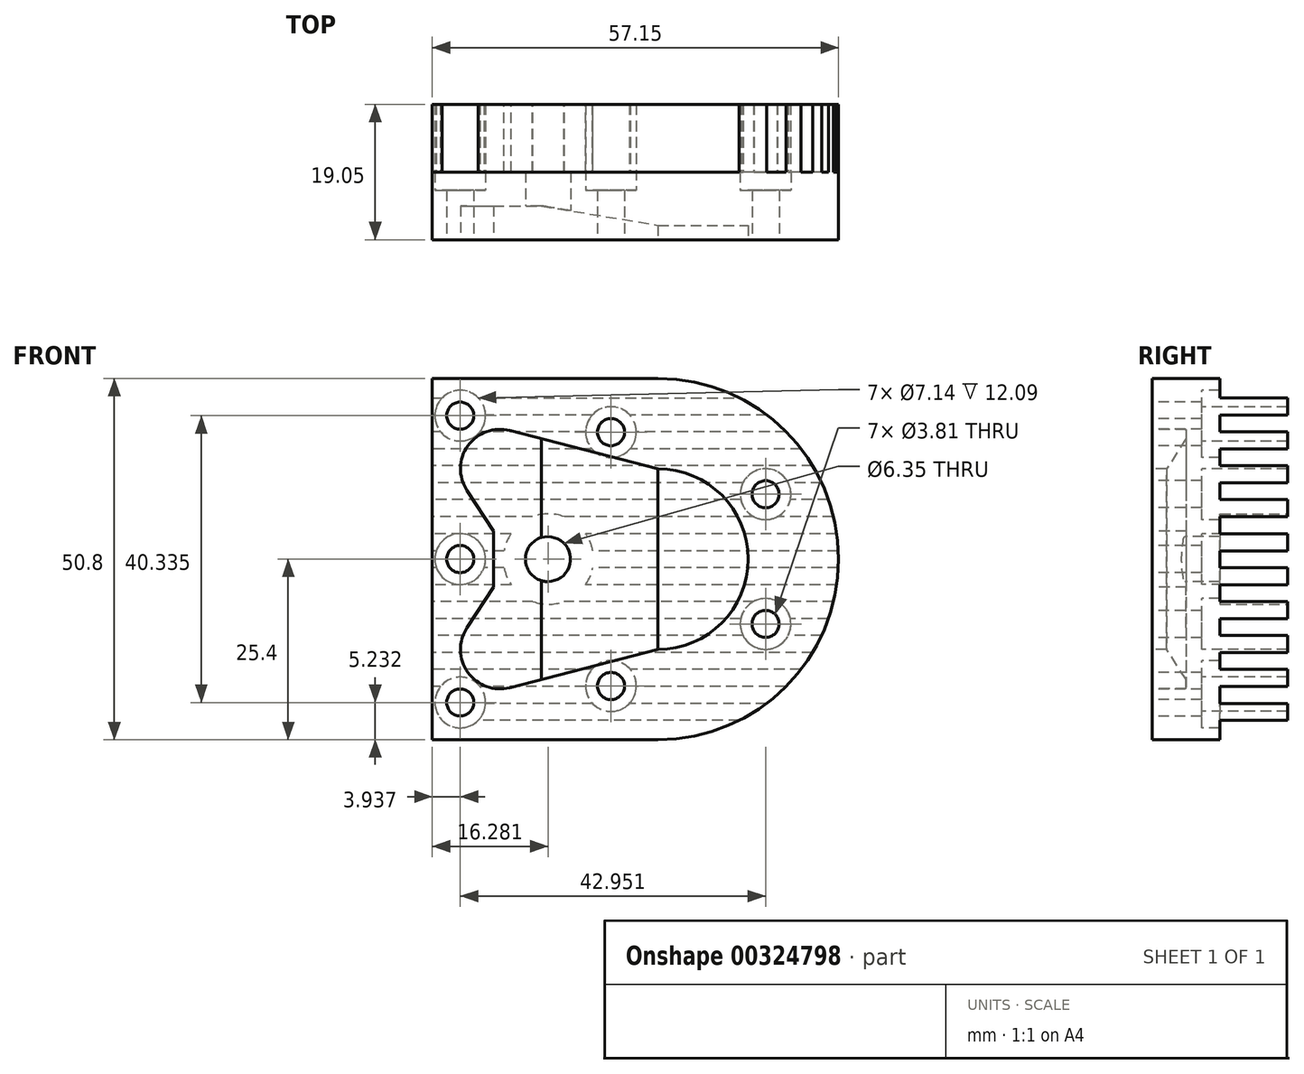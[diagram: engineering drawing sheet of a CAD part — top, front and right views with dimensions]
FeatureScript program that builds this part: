
annotation { "Feature Type Name" : "Feature", "Feature Type Description" : "" }
export const myFeature = defineFeature(function(context is Context, id is Id, definition is map)
    precondition{}
    {
        {
            var Q0;
            Q0=qCreatedBy(makeId("Front.planeOp"),FACE);
            var sketch = newSketch(context, id + "F0", { "sketchPlane" : qUnion([Q0])});
            skArc(sketch, "E0", {"start": v(0, -25.4) * mm, "mid": v(25.4, 0) * mm, "end": v(0, 25.4) * mm});
            skLineSegment(sketch, "E1", {"start": v(0, 25.4) * mm, "end": v(-31.75, 25.4) * mm});
            skLineSegment(sketch, "E2", {"start": v(0, -25.4) * mm, "end": v(-31.75, -25.4) * mm});
            skLineSegment(sketch, "E3", {"start": v(-31.75, 25.4) * mm, "end": v(-31.75, -25.4) * mm});
            skSolve(sketch);
        }
        {
            var Q0;
            Q0=makeQuery(id+"F0.imprint","IMPRINT",FACE,{"disambiguationData":[TD([[makeQuery(id+"F0.imprint","IMPRINT",EDGE,{"derivedFrom":sQuery(id+"F0.wireOp",EDGE,"E0")}),1.0]])]});
            extrude(context, id + "F1", {"entities" : qUnion([Q0]), "depth" : 19.05 * mm, "offsetDistance" : 25.4 * mm});
        }
        {
            var Q0;
            Q0=makeQuery(id+"F1.opExtrude","CAP_FACE",FACE,{"disambiguationData":[OSD([sQuery(id+"F0.wireOp",EDGE,"E0"),sQuery(id+"F0.wireOp",EDGE,"E1"),sQuery(id+"F0.wireOp",EDGE,"E2"),sQuery(id+"F0.wireOp",EDGE,"E3")])],"isStart":false});
            var sketch = newSketch(context, id + "F2", { "sketchPlane" : qUnion([Q0])});
            skArc(sketch, "E4", {"start": v(0, -12.7) * mm, "mid": v(12.7, 0) * mm, "end": v(0, 12.7) * mm});
            skLineSegment(sketch, "E5", {"start": v(0, 12.7) * mm, "end": v(0, -12.7) * mm});
            skSolve(sketch);
        }
        {
            var Q0;
            Q0=makeQuery(id+"F2.imprint","IMPRINT",FACE,{"disambiguationData":[TD([[makeQuery(id+"F2.imprint","IMPRINT",EDGE,{"derivedFrom":sQuery(id+"F2.wireOp",EDGE,"E4")}),1.0]])]});
            extrude(context, id + "F3", {"entities" : qUnion([Q0]), "operationType" : NewBodyOperationType.REMOVE, "oppositeDirection" : true, "depth" : 2.03 * mm, "offsetDistance" : 25.4 * mm});
        }
        {
            var Q0;
            Q0=makeQuery(id+"F3.boolean.opBoolean","COPY",EDGE,{"derivedFrom":makeQuery(id+"F3.opExtrude","CAP_EDGE",EDGE,{"disambiguationData":[OSD([sQuery(id+"F2.wireOp",EDGE,"E5")])],"isStart":false})});
            cPlane(context, id + "F4", {"entities" : qUnion([Q0]), "cplaneType" : CPlaneType.LINE_ANGLE, "offset" : 25.4 * mm, "angle" : 99.5 * degree, "width" : 152.4 * mm, "height" : 152.4 * mm});
        }
        {
            var Q0;
            Q0=makeQuery(id+"F1.opExtrude","CAP_FACE",FACE,{"disambiguationData":[OSD([sQuery(id+"F0.wireOp",EDGE,"E0"),sQuery(id+"F0.wireOp",EDGE,"E1"),sQuery(id+"F0.wireOp",EDGE,"E2"),sQuery(id+"F0.wireOp",EDGE,"E3")])],"isStart":false});
            var sketch = newSketch(context, id + "F5", { "sketchPlane" : qUnion([Q0])});
            skLineSegment(sketch, "E6", {"start": v(-22.23, 28.17) * mm, "end": v(-22.22, -26.85) * mm, "construction": true});
            skLineSegment(sketch, "E7", {"start": v(0, 12.7) * mm, "end": v(-42.37, 12.7) * mm, "construction": true});
            skLineSegment(sketch, "E8.MirrorCS", {"start": v(0, -12.7) * mm, "end": v(-42.37, -12.7) * mm, "construction": true});
            skArc(sketch, "E9", {"start": v(-20.84, 18.07) * mm, "mid": v(-26.74, 15.93) * mm, "end": v(-26.87, 9.66) * mm});
            skArc(sketch, "E10", {"start": v(-26.87, -9.66) * mm, "mid": v(-26.74, -15.93) * mm, "end": v(-20.84, -18.07) * mm});
            skLineSegment(sketch, "E11", {"start": v(-16.38, 30.43) * mm, "end": v(-16.38, -33.46) * mm, "construction": true});
            skLineSegment(sketch, "E12", {"start": v(-20.84, 18.07) * mm, "end": v(0, 12.7) * mm});
            skLineSegment(sketch, "E13.MirrorCS", {"start": v(-20.84, -18.07) * mm, "end": v(0, -12.7) * mm});
            skLineSegment(sketch, "E14", {"start": v(-23.11, 32.03) * mm, "end": v(-23.11, -31.77) * mm, "construction": true});
            skLineSegment(sketch, "E15", {"start": v(-23.11, 3.92) * mm, "end": v(-23.11, -3.92) * mm});
            skLineSegment(sketch, "E16", {"start": v(-26.87, 9.66) * mm, "end": v(-23.11, 3.92) * mm});
            skLineSegment(sketch, "E17.MirrorCS", {"start": v(-26.87, -9.66) * mm, "end": v(-23.11, -3.92) * mm});
            skLineSegment(sketch, "E18", {"start": v(-16.38, 16.92) * mm, "end": v(-16.38, -16.92) * mm});
            skSolve(sketch);
        }
        {
            var Q0;
            {var subQ4=sQuery(id+"F5.wireOp",EDGE,"E9");Q0=makeQuery(id+"F5.imprint","IMPRINT",FACE,{"disambiguationData":[TD([[makeQuery(id+"F5.imprint","IMPRINT",EDGE,{"derivedFrom":subQ4}),1.0]])]});}
            extrude(context, id + "F6", {"entities" : qUnion([Q0]), "operationType" : NewBodyOperationType.REMOVE, "oppositeDirection" : true, "depth" : 4.78 * mm, "offsetDistance" : 25.4 * mm});
        }
        {
            var Q0;
            {var subQ3=sQuery(id+"F5.wireOp",EDGE,"E18");Q0=makeQuery(id+"F5.imprint","IMPRINT",FACE,{"disambiguationData":[TD([[makeQuery(id+"F5.imprint","IMPRINT",EDGE,{"derivedFrom":subQ3}),1.0]])]});}
            var Q1;
            Q1=qCreatedBy(id+"F4.planeOp",FACE);
            extrude(context, id + "F7", {"entities" : qUnion([Q0]), "operationType" : NewBodyOperationType.REMOVE, "endBound" : BoundingType.UP_TO_SURFACE, "oppositeDirection" : true, "depth" : 25.4 * mm, "endBoundEntityFace" : qUnion([Q1]), "offsetDistance" : 25.4 * mm});
        }
        {
            var Q0;
            Q0=makeQuery(id+"F0.imprint","IMPRINT",FACE,{"disambiguationData":[TD([[makeQuery(id+"F0.imprint","IMPRINT",EDGE,{"derivedFrom":sQuery(id+"F0.wireOp",EDGE,"E0")}),1.0]])]});
            var sketch = newSketch(context, id + "F8", { "sketchPlane" : qUnion([Q0])});
            skPoint(sketch, "E19", {"position": v(-27.81, 20.17) * mm});
            skPoint(sketch, "E20", {"position": v(-6.6, 17.86) * mm});
            skPoint(sketch, "E21", {"position": v(15.14, 9.12) * mm});
            skPoint(sketch, "E22", {"position": v(15.14, -9.12) * mm});
            skPoint(sketch, "E23", {"position": v(-6.6, -17.86) * mm});
            skPoint(sketch, "E24", {"position": v(-27.81, -20.17) * mm});
            skPoint(sketch, "E25", {"position": v(-27.81, 0) * mm});
            skSolve(sketch);
        }
        {
            var Q0;
            Q0=sQuery(id+"F8.wireOp",VERTEX,"E19");
            var Q1;
            Q1=sQuery(id+"F8.wireOp",VERTEX,"E20");
            var Q2;
            Q2=sQuery(id+"F8.wireOp",VERTEX,"E21");
            var Q3;
            Q3=sQuery(id+"F8.wireOp",VERTEX,"E22");
            var Q4;
            Q4=sQuery(id+"F8.wireOp",VERTEX,"E23");
            var Q5;
            Q5=sQuery(id+"F8.wireOp",VERTEX,"E24");
            var Q6;
            Q6=sQuery(id+"F8.wireOp",VERTEX,"E25");
            var Q7;
            Q7=makeQuery(id+"F1.opExtrude","SWEPT_BODY",BODY,{"disambiguationData":[OSD([sQuery(id+"F0.wireOp",EDGE,"E0"),sQuery(id+"F0.wireOp",EDGE,"E1"),sQuery(id+"F0.wireOp",EDGE,"E2"),sQuery(id+"F0.wireOp",EDGE,"E3")])]});
            hole(context, id + "F9", {"style" : HoleStyle.C_BORE, "endStyle" : HoleEndStyle.THROUGH, "oppositeDirection" : true, "holeDiameter" : 3.8 * mm, "cBoreDiameter" : 7.14 * mm, "cBoreDepth" : 12.1 * mm, "majorDiameter" : 6.35 * mm, "tappedDepth" : 12.7 * mm, "tapClearance" : 3, "locations" : qUnion([Q0, Q1, Q2, Q3, Q4, Q5, Q6]), "scope" : qUnion([Q7])});
        }
        {
            var Q0;
            Q0=makeQuery(id+"F0.imprint","IMPRINT",FACE,{"disambiguationData":[TD([[makeQuery(id+"F0.imprint","IMPRINT",EDGE,{"derivedFrom":sQuery(id+"F0.wireOp",EDGE,"E0")}),1.0]])]});
            var sketch = newSketch(context, id + "F10", { "sketchPlane" : qUnion([Q0])});
            skPoint(sketch, "E26", {"position": v(-15.47, 0) * mm});
            skSolve(sketch);
        }
        {
            var Q0;
            Q0=sQuery(id+"F10.wireOp",VERTEX,"E26");
            var Q1;
            Q1=makeQuery(id+"F1.opExtrude","SWEPT_BODY",BODY,{"disambiguationData":[OSD([sQuery(id+"F0.wireOp",EDGE,"E0"),sQuery(id+"F0.wireOp",EDGE,"E1"),sQuery(id+"F0.wireOp",EDGE,"E2"),sQuery(id+"F0.wireOp",EDGE,"E3")])]});
            hole(context, id + "F11", {"style" : HoleStyle.SIMPLE, "endStyle" : HoleEndStyle.THROUGH, "oppositeDirection" : true, "holeDiameter" : 6.35 * mm, "majorDiameter" : 6.35 * mm, "tappedDepth" : 12.7 * mm, "tapClearance" : 3, "locations" : qUnion([Q0]), "scope" : qUnion([Q1])});
        }
        {
            var Q0;
            Q0=makeQuery(id+"F1.opExtrude","SWEPT_FACE",FACE,{"disambiguationData":[OSD([sQuery(id+"F0.wireOp",EDGE,"E3")])]});
            var sketch = newSketch(context, id + "F12", { "sketchPlane" : qUnion([Q0])});
            skLineSegment(sketch, "E27", {"start": v(9.53, 37.8) * mm, "end": v(9.53, -36.8) * mm, "construction": true});
            skLineSegment(sketch, "E28.bottom", {"start": v(-2.83, 1.17) * mm, "end": v(9.53, 1.17) * mm});
            skLineSegment(sketch, "E28.top", {"start": v(-2.83, -1.2) * mm, "end": v(9.53, -1.2) * mm});
            skLineSegment(sketch, "E28.left", {"start": v(-2.83, 1.17) * mm, "end": v(-2.83, -1.2) * mm});
            skLineSegment(sketch, "E29.0.1.0", {"start": v(-2.83, 3.58) * mm, "end": v(9.53, 3.58) * mm});
            skLineSegment(sketch, "E29.0.1.1", {"start": v(-2.83, 5.94) * mm, "end": v(9.53, 5.94) * mm});
            skLineSegment(sketch, "E29.0.1.2", {"start": v(-2.83, 5.94) * mm, "end": v(-2.83, 3.58) * mm});
            skLineSegment(sketch, "E29.0.2.0", {"start": v(-2.83, 8.36) * mm, "end": v(9.53, 8.36) * mm});
            skLineSegment(sketch, "E29.0.2.1", {"start": v(-2.83, 10.72) * mm, "end": v(9.53, 10.72) * mm});
            skLineSegment(sketch, "E29.0.2.2", {"start": v(-2.83, 10.72) * mm, "end": v(-2.83, 8.36) * mm});
            skLineSegment(sketch, "E29.0.3.0", {"start": v(-2.83, 13.13) * mm, "end": v(9.53, 13.13) * mm});
            skLineSegment(sketch, "E29.0.3.1", {"start": v(-2.83, 15.5) * mm, "end": v(9.53, 15.5) * mm});
            skLineSegment(sketch, "E29.0.3.2", {"start": v(-2.83, 15.5) * mm, "end": v(-2.83, 13.13) * mm});
            skLineSegment(sketch, "E29.0.4.0", {"start": v(-2.83, 17.9) * mm, "end": v(9.53, 17.9) * mm});
            skLineSegment(sketch, "E29.0.4.1", {"start": v(-2.83, 20.27) * mm, "end": v(9.53, 20.27) * mm});
            skLineSegment(sketch, "E29.0.4.2", {"start": v(-2.83, 20.27) * mm, "end": v(-2.83, 17.9) * mm});
            skLineSegment(sketch, "E29.direction1", {"start": v(-2.83, -1.2) * mm, "end": v(9.53, -1.2) * mm, "construction": true});
            skLineSegment(sketch, "E29.direction2", {"start": v(-2.83, -1.2) * mm, "end": v(-2.83, 3.58) * mm, "construction": true});
            skLineSegment(sketch, "E30.bottom", {"start": v(-2.83, 27.58) * mm, "end": v(9.53, 27.58) * mm});
            skLineSegment(sketch, "E30.top", {"start": v(-2.83, 22.68) * mm, "end": v(9.53, 22.68) * mm});
            skLineSegment(sketch, "E30.left", {"start": v(-2.83, 27.58) * mm, "end": v(-2.83, 22.68) * mm});
            skPoint(sketch, "E31.orphan", {"position": v(22.57, -1.2) * mm});
            skLineSegment(sketch, "E32", {"start": v(9.53, 27.58) * mm, "end": v(9.53, 22.68) * mm});
            skLineSegment(sketch, "E33", {"start": v(9.53, 20.27) * mm, "end": v(9.53, 17.9) * mm});
            skLineSegment(sketch, "E34", {"start": v(9.53, -1.2) * mm, "end": v(9.53, 1.17) * mm});
            skLineSegment(sketch, "E35", {"start": v(9.53, 3.58) * mm, "end": v(9.53, 5.94) * mm});
            skLineSegment(sketch, "E36", {"start": v(9.53, 8.36) * mm, "end": v(9.53, 10.72) * mm});
            skLineSegment(sketch, "E37", {"start": v(9.53, 13.13) * mm, "end": v(9.53, 15.5) * mm});
            skLineSegment(sketch, "E38.MirrorCS", {"start": v(-2.83, -22.68) * mm, "end": v(9.53, -22.68) * mm});
            skLineSegment(sketch, "E39.MirrorCS", {"start": v(-2.83, -27.58) * mm, "end": v(-2.83, -22.68) * mm});
            skLineSegment(sketch, "E40.MirrorCS", {"start": v(-2.83, -27.58) * mm, "end": v(9.53, -27.58) * mm});
            skLineSegment(sketch, "E41.MirrorCS", {"start": v(9.53, -27.58) * mm, "end": v(9.53, -22.68) * mm});
            skLineSegment(sketch, "E42.0.1.0", {"start": v(-2.83, -3.6) * mm, "end": v(9.53, -3.6) * mm});
            skLineSegment(sketch, "E42.0.1.1", {"start": v(-2.83, -3.6) * mm, "end": v(-2.83, -5.97) * mm});
            skLineSegment(sketch, "E42.0.1.2", {"start": v(9.53, -5.97) * mm, "end": v(9.53, -3.6) * mm});
            skLineSegment(sketch, "E42.0.1.3", {"start": v(-2.83, -5.97) * mm, "end": v(9.53, -5.97) * mm, "construction": true});
            skLineSegment(sketch, "E42.0.1.4", {"start": v(-2.83, -5.97) * mm, "end": v(9.53, -5.97) * mm});
            skLineSegment(sketch, "E42.0.2.0", {"start": v(-2.83, -8.38) * mm, "end": v(9.53, -8.38) * mm});
            skLineSegment(sketch, "E42.0.2.1", {"start": v(-2.83, -8.38) * mm, "end": v(-2.83, -10.74) * mm});
            skLineSegment(sketch, "E42.0.2.2", {"start": v(9.53, -10.74) * mm, "end": v(9.53, -8.38) * mm});
            skLineSegment(sketch, "E42.0.2.3", {"start": v(-2.83, -10.74) * mm, "end": v(9.53, -10.74) * mm, "construction": true});
            skLineSegment(sketch, "E42.0.2.4", {"start": v(-2.83, -10.74) * mm, "end": v(9.53, -10.74) * mm});
            skLineSegment(sketch, "E42.0.3.0", {"start": v(-2.83, -13.16) * mm, "end": v(9.53, -13.16) * mm});
            skLineSegment(sketch, "E42.0.3.1", {"start": v(-2.83, -13.16) * mm, "end": v(-2.83, -15.52) * mm});
            skLineSegment(sketch, "E42.0.3.2", {"start": v(9.53, -15.52) * mm, "end": v(9.53, -13.16) * mm});
            skLineSegment(sketch, "E42.0.3.3", {"start": v(-2.83, -15.52) * mm, "end": v(9.53, -15.52) * mm, "construction": true});
            skLineSegment(sketch, "E42.0.3.4", {"start": v(-2.83, -15.52) * mm, "end": v(9.53, -15.52) * mm});
            skLineSegment(sketch, "E42.0.4.0", {"start": v(-2.83, -17.93) * mm, "end": v(9.53, -17.93) * mm});
            skLineSegment(sketch, "E42.0.4.1", {"start": v(-2.83, -17.93) * mm, "end": v(-2.83, -20.3) * mm});
            skLineSegment(sketch, "E42.0.4.2", {"start": v(9.53, -20.3) * mm, "end": v(9.53, -17.93) * mm});
            skLineSegment(sketch, "E42.0.4.3", {"start": v(-2.83, -20.3) * mm, "end": v(9.53, -20.3) * mm, "construction": true});
            skLineSegment(sketch, "E42.0.4.4", {"start": v(-2.83, -20.3) * mm, "end": v(9.53, -20.3) * mm});
            skLineSegment(sketch, "E42.direction1", {"start": v(-2.83, -1.2) * mm, "end": v(22.57, -1.2) * mm, "construction": true});
            skLineSegment(sketch, "E42.direction2", {"start": v(-2.83, -1.2) * mm, "end": v(-2.83, -5.97) * mm, "construction": true});
            skSolve(sketch);
        }
        {
            var Q0;
            {var subQ0=sQuery(id+"F12.wireOp",EDGE,"E32");var subQ1=sQuery(id+"F12.wireOp",EDGE,"E30.top");var subQ2=makeQuery(id+"F12.imprint","INTERSECT",VERTEX,{"derivedFrom":[subQ1,subQ0]});Q0=makeQuery(id+"F12.imprint","IMPRINT",FACE,{"disambiguationData":[TD([[makeQuery(id+"F12.imprint","IMPRINT",EDGE,{"disambiguationData":[TD([[subQ2,1.0]])],"derivedFrom":subQ1}),1.0]])]});}
            var Q1;
            {var subQ1=sQuery(id+"F12.wireOp",EDGE,"E30.bottom");Q1=makeQuery(id+"F12.imprint","IMPRINT",FACE,{"disambiguationData":[TD([[makeQuery(id+"F12.imprint","IMPRINT",EDGE,{"derivedFrom":subQ1}),-1.0]])]});}
            var Q2;
            {var subQ0=sQuery(id+"F12.wireOp",EDGE,"E33");Q2=makeQuery(id+"F12.imprint","IMPRINT",FACE,{"disambiguationData":[TD([[makeQuery(id+"F12.imprint","IMPRINT",EDGE,{"derivedFrom":subQ0}),-1.0]])]});}
            var Q3;
            {var subQ0=sQuery(id+"F12.wireOp",EDGE,"E37");Q3=makeQuery(id+"F12.imprint","IMPRINT",FACE,{"disambiguationData":[TD([[makeQuery(id+"F12.imprint","IMPRINT",EDGE,{"derivedFrom":subQ0}),1.0]])]});}
            var Q4;
            {var subQ0=sQuery(id+"F12.wireOp",EDGE,"E36");Q4=makeQuery(id+"F12.imprint","IMPRINT",FACE,{"disambiguationData":[TD([[makeQuery(id+"F12.imprint","IMPRINT",EDGE,{"derivedFrom":subQ0}),1.0]])]});}
            var Q5;
            {var subQ0=sQuery(id+"F12.wireOp",EDGE,"E35");Q5=makeQuery(id+"F12.imprint","IMPRINT",FACE,{"disambiguationData":[TD([[makeQuery(id+"F12.imprint","IMPRINT",EDGE,{"derivedFrom":subQ0}),1.0]])]});}
            var Q6;
            {var subQ0=sQuery(id+"F12.wireOp",EDGE,"E34");Q6=makeQuery(id+"F12.imprint","IMPRINT",FACE,{"disambiguationData":[TD([[makeQuery(id+"F12.imprint","IMPRINT",EDGE,{"derivedFrom":subQ0}),1.0]])]});}
            var Q7;
            {var subQ0=sQuery(id+"F12.wireOp",EDGE,"E42.0.1.2");Q7=makeQuery(id+"F12.imprint","IMPRINT",FACE,{"disambiguationData":[TD([[makeQuery(id+"F12.imprint","IMPRINT",EDGE,{"derivedFrom":subQ0}),1.0]])]});}
            var Q8;
            {var subQ0=sQuery(id+"F12.wireOp",EDGE,"E42.0.2.2");Q8=makeQuery(id+"F12.imprint","IMPRINT",FACE,{"disambiguationData":[TD([[makeQuery(id+"F12.imprint","IMPRINT",EDGE,{"derivedFrom":subQ0}),1.0]])]});}
            var Q9;
            {var subQ0=sQuery(id+"F12.wireOp",EDGE,"E42.0.3.2");Q9=makeQuery(id+"F12.imprint","IMPRINT",FACE,{"disambiguationData":[TD([[makeQuery(id+"F12.imprint","IMPRINT",EDGE,{"derivedFrom":subQ0}),1.0]])]});}
            var Q10;
            {var subQ0=sQuery(id+"F12.wireOp",EDGE,"E42.0.4.2");Q10=makeQuery(id+"F12.imprint","IMPRINT",FACE,{"disambiguationData":[TD([[makeQuery(id+"F12.imprint","IMPRINT",EDGE,{"derivedFrom":subQ0}),1.0]])]});}
            var Q11;
            {var subQ0=sQuery(id+"F12.wireOp",EDGE,"E41.MirrorCS");var subQ1=sQuery(id+"F12.wireOp",EDGE,"E38.MirrorCS");var subQ2=makeQuery(id+"F12.imprint","INTERSECT",VERTEX,{"derivedFrom":[subQ1,subQ0]});Q11=makeQuery(id+"F12.imprint","IMPRINT",FACE,{"disambiguationData":[TD([[makeQuery(id+"F12.imprint","IMPRINT",EDGE,{"disambiguationData":[TD([[subQ2,1.0]])],"derivedFrom":subQ1}),-1.0]])]});}
            extrude(context, id + "F13", {"entities" : qUnion([Q0, Q1, Q2, Q3, Q4, Q5, Q6, Q7, Q8, Q9, Q10, Q11]), "operationType" : NewBodyOperationType.REMOVE, "endBound" : BoundingType.THROUGH_ALL, "oppositeDirection" : true, "depth" : 25.4 * mm, "offsetDistance" : 25.4 * mm});
        }
        {
            var Q0;
            Q0=makeQuery(id+"F8.imprint","IMPRINT",FACE,{"disambiguationData":[TD([[makeQuery(id+"F8.imprint","IMPRINT",EDGE,{"derivedFrom":makeQuery(id+"F0.imprint","IMPRINT",EDGE,{"derivedFrom":sQuery(id+"F0.wireOp",EDGE,"E0")})}),1.0]])]});
            var sketch = newSketch(context, id + "F14", { "sketchPlane" : qUnion([Q0])});
            skCircle(sketch, "E43", {"center": v(-15.41, 0) * mm, "radius": 6.35 * mm});
            skSolve(sketch);
        }
        {
            var Q0;
            Q0=makeQuery(id+"F14.imprint","IMPRINT",FACE,{"disambiguationData":[TD([[makeQuery(id+"F14.imprint","IMPRINT",EDGE,{"derivedFrom":sQuery(id+"F14.wireOp",EDGE,"E43")}),1.0]])]});
            extrude(context, id + "F15", {"entities" : qUnion([Q0]), "operationType" : NewBodyOperationType.REMOVE, "depth" : 9.52 * mm, "offsetDistance" : 25.4 * mm});
        }
        {
            var Q0;
            Q0=makeQuery(id+"F1.opExtrude","SWEPT_FACE",FACE,{"disambiguationData":[OSD([sQuery(id+"F0.wireOp",EDGE,"E3")])]});
            var sketch = newSketch(context, id + "F16", { "sketchPlane" : qUnion([Q0])});
            skLineSegment(sketch, "E44.bottom", {"start": v(9.53, 20.27) * mm, "end": v(-1.19, 20.27) * mm});
            skLineSegment(sketch, "E44.top", {"start": v(9.53, 23.42) * mm, "end": v(-1.19, 23.42) * mm});
            skLineSegment(sketch, "E44.left", {"start": v(9.53, 20.27) * mm, "end": v(9.53, 23.42) * mm});
            skLineSegment(sketch, "E44.right", {"start": v(-1.19, 20.27) * mm, "end": v(-1.19, 23.42) * mm});
            skPoint(sketch, "E45.oppositeSnap0", {"position": v(4.76, -22.68) * mm});
            skLineSegment(sketch, "E45.bottom", {"start": v(9.53, -20.3) * mm, "end": v(-0.56, -20.3) * mm});
            skLineSegment(sketch, "E45.top", {"start": v(9.53, -22.68) * mm, "end": v(-0.56, -22.68) * mm});
            skLineSegment(sketch, "E45.left", {"start": v(9.53, -20.3) * mm, "end": v(9.53, -22.68) * mm});
            skLineSegment(sketch, "E45.right", {"start": v(-0.56, -20.3) * mm, "end": v(-0.56, -22.68) * mm});
            skSolve(sketch);
        }
        {
            var Q0;
            {var subQ4=sQuery(id+"F12.wireOp",EDGE,"E30.top");var subQ6=makeQuery(id+"F13.boolean.opBoolean","COPY",EDGE,{"derivedFrom":makeQuery(id+"F13.opExtrude","CAP_EDGE",EDGE,{"disambiguationData":[OSD([subQ4])],"isStart":true})});Q0=makeQuery(id+"F16.imprint","IMPRINT",FACE,{"disambiguationData":[TD([[makeQuery(id+"F16.imprint","IMPRINT",EDGE,{"derivedFrom":subQ6}),-1.0]])]});}
            var Q1;
            {var subQ0=sQuery(id+"F16.wireOp",EDGE,"E45.left");Q1=makeQuery(id+"F16.imprint","IMPRINT",FACE,{"disambiguationData":[TD([[makeQuery(id+"F16.imprint","IMPRINT",EDGE,{"derivedFrom":subQ0}),-1.0]])]});}
            extrude(context, id + "F17", {"entities" : qUnion([Q0, Q1]), "operationType" : NewBodyOperationType.REMOVE, "oppositeDirection" : true, "depth" : 5.08 * mm, "offsetDistance" : 25.4 * mm});
        }
    });
